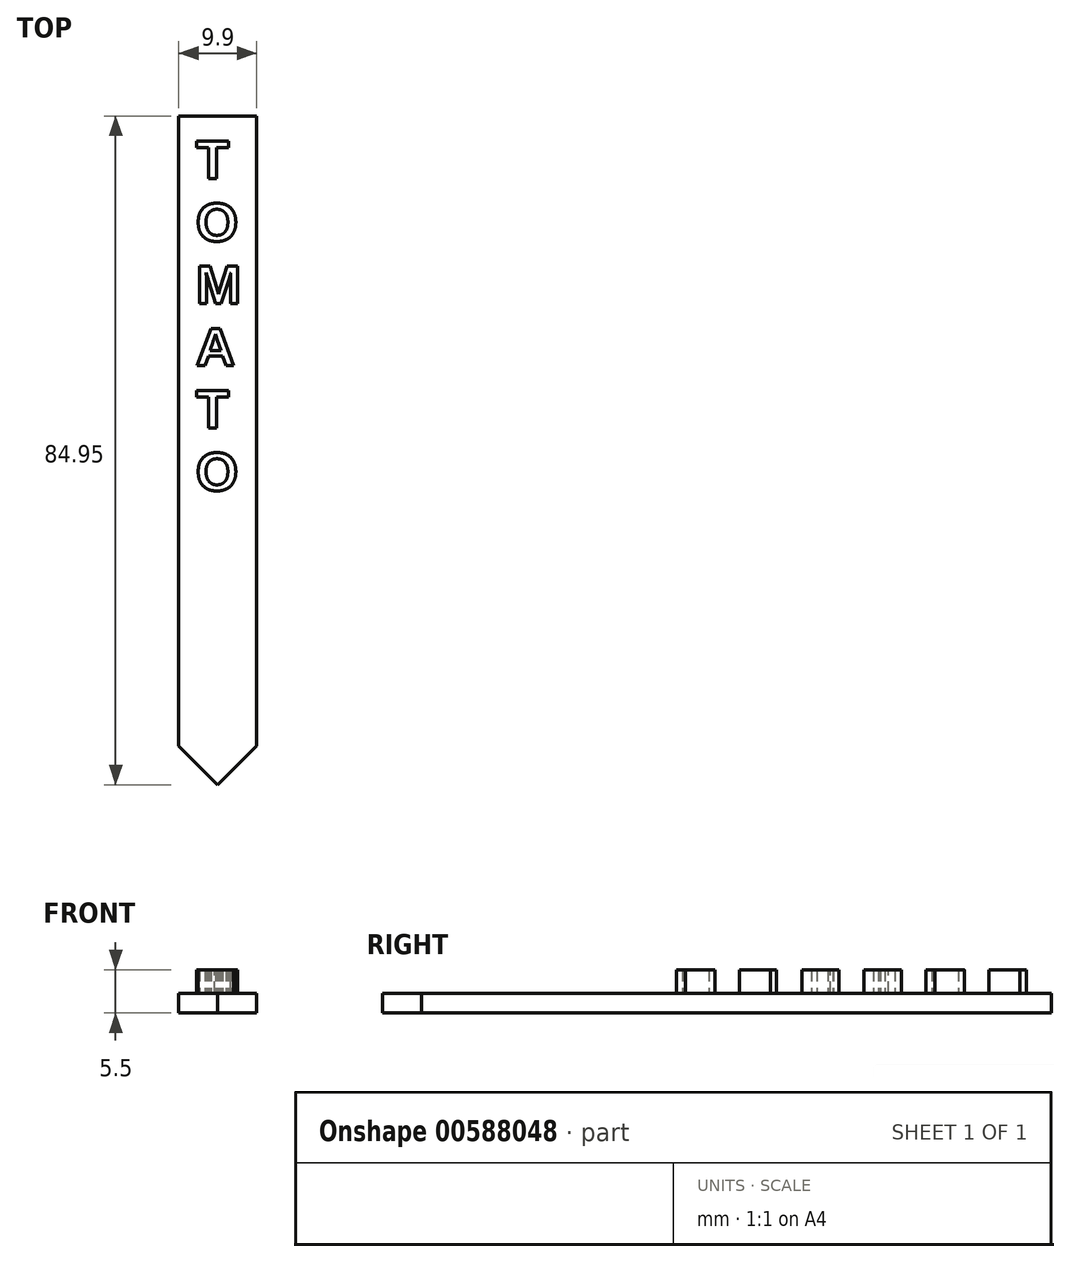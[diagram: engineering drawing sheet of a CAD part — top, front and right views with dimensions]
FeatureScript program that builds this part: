
annotation { "Feature Type Name" : "Feature", "Feature Type Description" : "" }
export const myFeature = defineFeature(function(context is Context, id is Id, definition is map)
    precondition{}
    {
        {
            var Q0;
            Q0=qCreatedBy(makeId("Top.planeOp"),FACE);
            var sketch = newSketch(context, id + "F0", { "sketchPlane" : qUnion([Q0])});
            skLineSegment(sketch, "E0", {"start": v(0, 0) * mm, "end": v(4.95, 4.95) * mm});
            skLineSegment(sketch, "E1", {"start": v(0, 0) * mm, "end": v(-4.95, 4.95) * mm});
            skPoint(sketch, "E2.end.orphan", {"position": v(-3.53, 0) * mm});
            skPoint(sketch, "E3.end.orphan", {"position": v(4.95, 0) * mm});
            skLineSegment(sketch, "E4", {"start": v(4.95, 4.95) * mm, "end": v(4.95, 84.95) * mm});
            skLineSegment(sketch, "E5", {"start": v(-4.95, 4.95) * mm, "end": v(-4.95, 84.95) * mm});
            skLineSegment(sketch, "E6", {"start": v(-4.95, 84.95) * mm, "end": v(4.95, 84.95) * mm});
            skSolve(sketch);
        }
        {
            var Q0;
            Q0=qSketchRegion(id+"F0",true);
            extrude(context, id + "F1", {"entities" : qUnion([Q0]), "depth" : 2.5 * mm, "offsetDistance" : 25 * mm});
        }
        {
            var Q0;
            Q0=makeQuery(id+"F1.opExtrude","CAP_FACE",FACE,{"disambiguationData":[OSD([sQuery(id+"F0.wireOp",EDGE,"E0"),sQuery(id+"F0.wireOp",EDGE,"E1"),sQuery(id+"F0.wireOp",EDGE,"E4"),sQuery(id+"F0.wireOp",EDGE,"E5"),sQuery(id+"F0.wireOp",EDGE,"E6")])],"isStart":false});
            var sketch = newSketch(context, id + "F2", { "sketchPlane" : qUnion([Q0])});
            skText(sketch, "E7", { "text": "T\nO\nM\nA\nT\nO", "fontName": "Arimo-Bold.ttf"});
            const initialGuessF2  = {"E7": [-0.00277, 0.077, 1, 0, 0.00496]};
            skSetInitialGuess(sketch, initialGuessF2);
            skSolve(sketch);
        }
        {
            var Q0;
            Q0=qSketchRegion(id+"F2",true);
            extrude(context, id + "F3", {"entities" : qUnion([Q0]), "operationType" : NewBodyOperationType.ADD, "depth" : 3 * mm, "offsetDistance" : 25 * mm});
        }
    });
